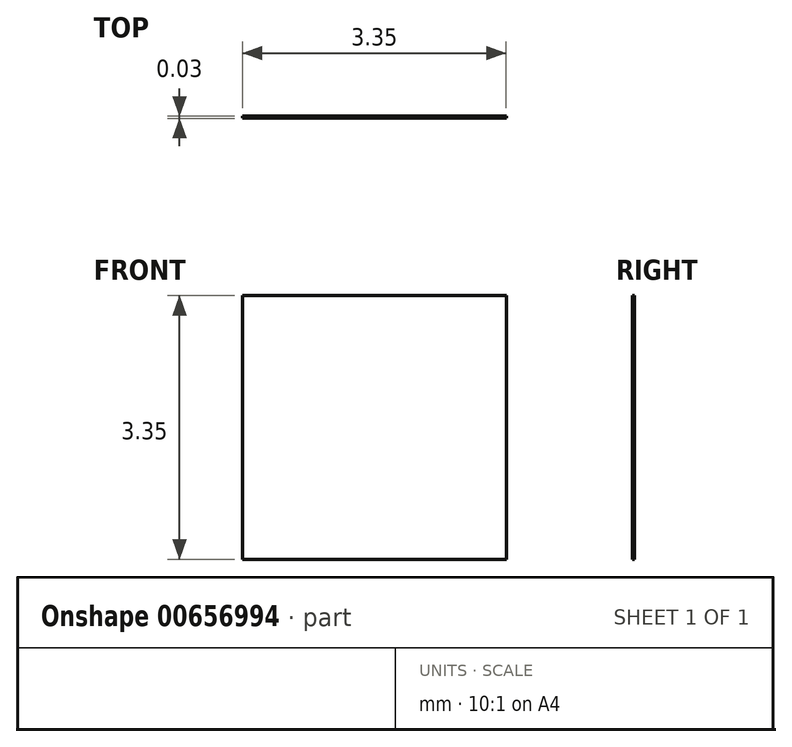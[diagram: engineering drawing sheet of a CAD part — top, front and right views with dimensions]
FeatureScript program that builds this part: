
annotation { "Feature Type Name" : "Feature", "Feature Type Description" : "" }
export const myFeature = defineFeature(function(context is Context, id is Id, definition is map)
    precondition{}
    {
        {
            var Q0;
            Q0=qCreatedBy(makeId("Front.planeOp"),FACE);
            var sketch = newSketch(context, id + "F0", { "sketchPlane" : qUnion([Q0])});
            skLineSegment(sketch, "E0", {"start": v(0, 2.33) * mm, "end": v(0, -1.02) * mm});
            skLineSegment(sketch, "E1", {"start": v(0, -1.02) * mm, "end": v(3.35, -1.02) * mm});
            skLineSegment(sketch, "E2", {"start": v(3.35, -1.02) * mm, "end": v(3.35, 2.33) * mm});
            skLineSegment(sketch, "E3", {"start": v(3.35, 2.33) * mm, "end": v(0, 2.33) * mm});
            skSolve(sketch);
        }
        {
            var Q0;
            Q0 = qSketchRegion(id + "F0", true);
            extrude(context, id + "F1", {"entities" : qUnion([Q0]), "depth" : 0.03 * mm, "offsetDistance" : 25.4 * mm});
        }
    });
